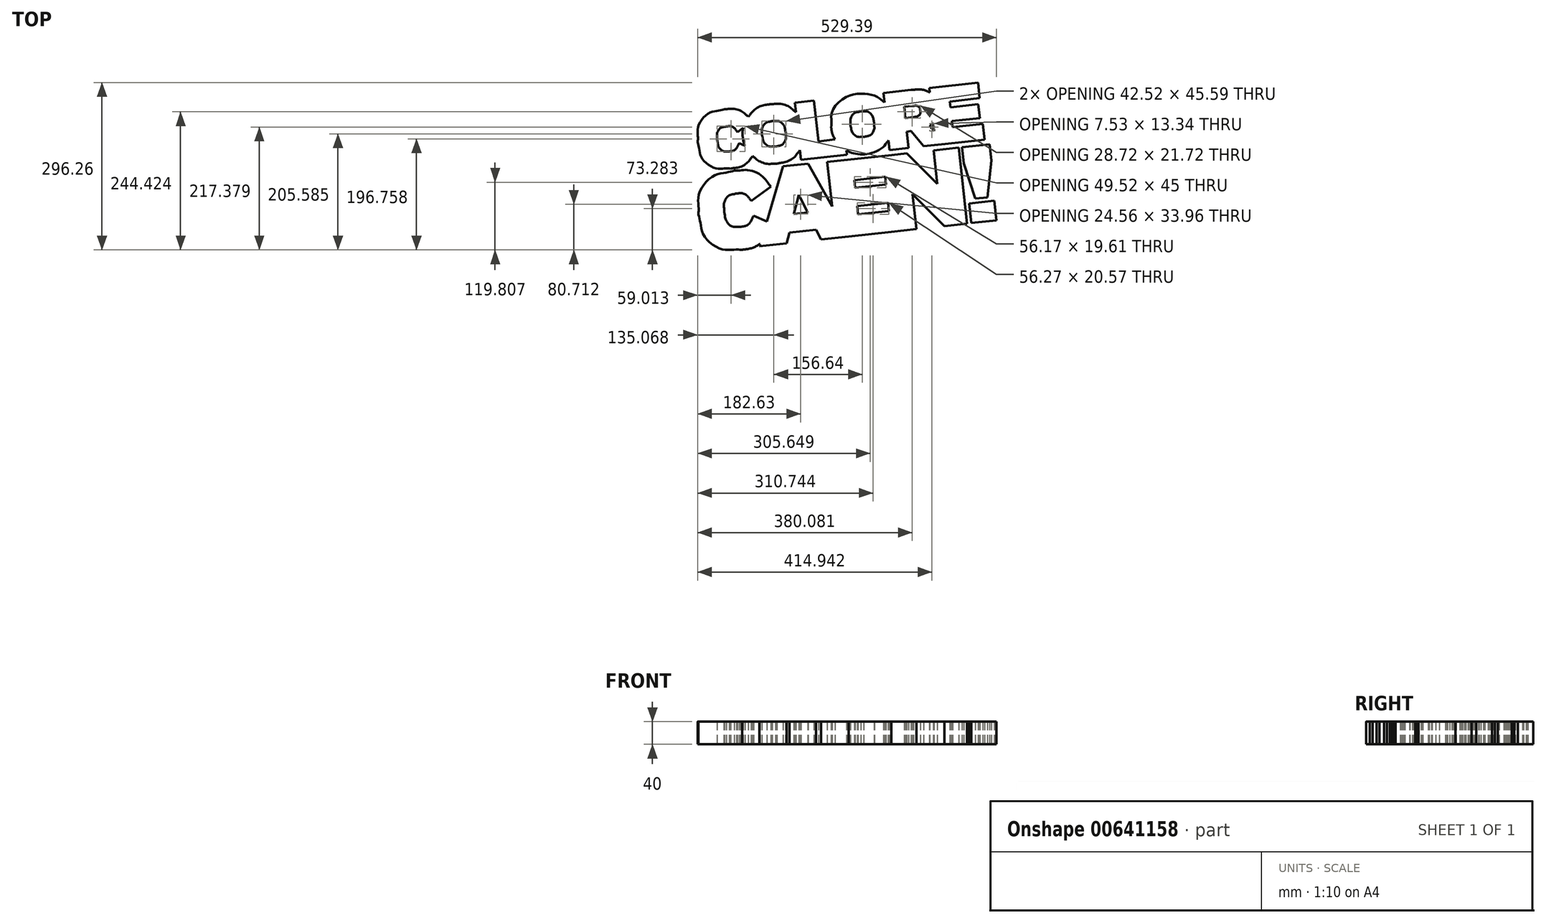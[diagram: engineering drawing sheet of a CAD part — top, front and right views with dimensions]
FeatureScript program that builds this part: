
annotation { "Feature Type Name" : "Feature", "Feature Type Description" : "" }
export const myFeature = defineFeature(function(context is Context, id is Id, definition is map)
    precondition{}
    {
        {
            var Q0;
            Q0=qCreatedBy(makeId("Top.planeOp"),FACE);
            var sketch = newSketch(context, id + "F0", { "sketchPlane" : qUnion([Q0])});
            skLineSegment(sketch, "E0", {"start": v(-194.16, 60.47) * mm, "end": v(-183.95, 68.05) * mm});
            skFitSpline(sketch, "E1", {"points": [v(-213.82, 70.72) * mm, v(-211.03, 70.75) * mm, v(-205.74, 70.82) * mm, v(-198.74, 66.62) * mm, v(-195.71, 62.55) * mm, v(-194.16, 60.47) * mm]});
            skLineSegment(sketch, "E2", {"start": v(-184.83, 51.27) * mm, "end": v(-184.8, 50.98) * mm});
            skFitSpline(sketch, "E3", {"points": [v(-183.95, 68.05) * mm, v(-184.28, 66.24) * mm, v(-184.96, 62.58) * mm, v(-185.27, 56.95) * mm, v(-184.98, 53.18) * mm, v(-184.83, 51.27) * mm]});
            skLineSegment(sketch, "E4", {"start": v(-181.03, 36.4) * mm, "end": v(-191.27, 40.79) * mm});
            skFitSpline(sketch, "E5", {"points": [v(-184.8, 50.98) * mm, v(-184.56, 49.29) * mm, v(-184.1, 45.93) * mm, v(-182.83, 41.04) * mm, v(-181.63, 37.93) * mm, v(-181.03, 36.4) * mm]});
            skFitSpline(sketch, "E6", {"points": [v(-191.27, 40.79) * mm, v(-192.44, 38.32) * mm, v(-194.69, 33.56) * mm, v(-200.78, 27.71) * mm, v(-206.11, 26.6) * mm, v(-208.92, 26) * mm]});
            skLineSegment(sketch, "E7", {"start": v(-230.26, 46.3) * mm, "end": v(-230.3, 46.58) * mm});
            skFitSpline(sketch, "E8", {"points": [v(-208.92, 26) * mm, v(-212.45, 26.2) * mm, v(-219.53, 26.57) * mm, v(-227.86, 35.01) * mm, v(-229.43, 42.36) * mm, v(-230.26, 46.3) * mm]});
            skFitSpline(sketch, "E9", {"points": [v(-230.3, 46.58) * mm, v(-230.3, 50.43) * mm, v(-230.28, 57.75) * mm, v(-224.15, 67.74) * mm, v(-217.27, 69.73) * mm, v(-213.82, 70.72) * mm]});
            skLineSegment(sketch, "E10", {"start": v(-108.67, 59.61) * mm, "end": v(-108.64, 59.32) * mm});
            skFitSpline(sketch, "E11", {"points": [v(-132.37, 80.08) * mm, v(-128.34, 79.88) * mm, v(-120.5, 79.49) * mm, v(-111.39, 70.87) * mm, v(-109.59, 63.41) * mm, v(-108.67, 59.61) * mm]});
            skFitSpline(sketch, "E12", {"points": [v(-108.64, 59.32) * mm, v(-108.7, 55.46) * mm, v(-108.84, 47.9) * mm, v(-115.77, 37.63) * mm, v(-123.25, 35.59) * mm, v(-127.1, 34.53) * mm]});
            skLineSegment(sketch, "E13", {"start": v(-150.8, 55) * mm, "end": v(-150.82, 55.29) * mm});
            skFitSpline(sketch, "E14", {"points": [v(-127.1, 34.53) * mm, v(-131.12, 34.73) * mm, v(-138.96, 35.12) * mm, v(-148.08, 43.74) * mm, v(-149.87, 51.2) * mm, v(-150.8, 55) * mm]});
            skFitSpline(sketch, "E15", {"points": [v(-150.82, 55.29) * mm, v(-150.76, 59.15) * mm, v(-150.62, 66.72) * mm, v(-143.7, 76.98) * mm, v(-136.22, 79.03) * mm, v(-132.37, 80.08) * mm]});
            skLineSegment(sketch, "E16", {"start": v(47.97, 76.77) * mm, "end": v(48, 76.48) * mm});
            skFitSpline(sketch, "E17", {"points": [v(24.27, 97.23) * mm, v(28.3, 97.03) * mm, v(36.14, 96.64) * mm, v(45.25, 88.03) * mm, v(47.05, 80.57) * mm, v(47.97, 76.77) * mm]});
            skFitSpline(sketch, "E18", {"points": [v(48, 76.48) * mm, v(47.93, 72.62) * mm, v(47.8, 65.05) * mm, v(40.87, 54.79) * mm, v(33.4, 52.74) * mm, v(29.55, 51.69) * mm]});
            skLineSegment(sketch, "E19", {"start": v(5.85, 72.15) * mm, "end": v(5.82, 72.44) * mm});
            skFitSpline(sketch, "E20", {"points": [v(29.55, 51.69) * mm, v(25.52, 51.89) * mm, v(17.68, 52.28) * mm, v(8.56, 60.9) * mm, v(6.77, 68.35) * mm, v(5.85, 72.15) * mm]});
            skFitSpline(sketch, "E21", {"points": [v(5.82, 72.44) * mm, v(5.88, 76.3) * mm, v(6.02, 83.87) * mm, v(12.95, 94.13) * mm, v(20.42, 96.18) * mm, v(24.27, 97.23) * mm]});
            skLineSegment(sketch, "E22", {"start": v(129.53, 98.4) * mm, "end": v(129.56, 98.1) * mm});
            skFitSpline(sketch, "E23", {"points": [v(115.64, 106.66) * mm, v(117.94, 106.78) * mm, v(122.1, 107) * mm, v(128.04, 104.07) * mm, v(129.03, 100.3) * mm, v(129.53, 98.4) * mm]});
            skLineSegment(sketch, "E24", {"start": v(117.66, 86.88) * mm, "end": v(103.09, 85.28) * mm});
            skLineSegment(sketch, "E25", {"start": v(103.09, 85.28) * mm, "end": v(100.92, 105.05) * mm});
            skLineSegment(sketch, "E26", {"start": v(100.92, 105.05) * mm, "end": v(115.64, 106.66) * mm});
            skLineSegment(sketch, "E27", {"start": v(152.45, 75.77) * mm, "end": v(153.9, 62.43) * mm});
            skLineSegment(sketch, "E28", {"start": v(153.9, 62.43) * mm, "end": v(146.38, 71.2) * mm});
            skFitSpline(sketch, "E29", {"points": [v(129.56, 98.1) * mm, v(129.48, 96.18) * mm, v(129.3, 92.32) * mm, v(124.19, 88.01) * mm, v(120, 87.29) * mm, v(117.66, 86.88) * mm]});
            skFitSpline(sketch, "E30", {"points": [v(146.38, 71.2) * mm, v(147.1, 71.66) * mm, v(148.53, 72.6) * mm, v(150.56, 74.12) * mm, v(151.82, 75.22) * mm, v(152.45, 75.77) * mm]});
            skFitSpline(sketch, "E31", {"points": [v(-206.47, -4.38) * mm, v(-200.69, -3.35) * mm, v(-190, -1.46) * mm, v(-176.33, 6.53) * mm, v(-170.32, 14.02) * mm, v(-167.44, 17.61) * mm]});
            skFitSpline(sketch, "E32", {"points": [v(-167.44, 17.61) * mm, v(-163.43, 14.68) * mm, v(-155.28, 8.71) * mm, v(-140.1, 4.13) * mm, v(-129.54, 4.47) * mm, v(-124.1, 4.64) * mm]});
            skLineSegment(sketch, "E33", {"start": v(-83.36, 28.4) * mm, "end": v(-81.5, 11.5) * mm});
            skLineSegment(sketch, "E34", {"start": v(-81.5, 11.5) * mm, "end": v(-0.3, 20.4) * mm});
            skLineSegment(sketch, "E35", {"start": v(-0.3, 20.4) * mm, "end": v(-1.14, 28.1) * mm});
            skFitSpline(sketch, "E36", {"points": [v(-124.1, 4.64) * mm, v(-118.54, 5.71) * mm, v(-107.7, 7.8) * mm, v(-93.39, 16.22) * mm, v(-86.67, 24.39) * mm, v(-83.36, 28.4) * mm]});
            skLineSegment(sketch, "E37", {"start": v(73.28, 45.56) * mm, "end": v(75.13, 28.65) * mm});
            skLineSegment(sketch, "E38", {"start": v(75.13, 28.65) * mm, "end": v(108.88, 32.35) * mm});
            skLineSegment(sketch, "E39", {"start": v(108.88, 32.35) * mm, "end": v(105.73, 61.2) * mm});
            skLineSegment(sketch, "E40", {"start": v(105.73, 61.2) * mm, "end": v(112.65, 61.95) * mm});
            skLineSegment(sketch, "E41", {"start": v(112.65, 61.95) * mm, "end": v(112.94, 61.99) * mm});
            skLineSegment(sketch, "E42", {"start": v(112.94, 61.99) * mm, "end": v(135.14, 35.22) * mm});
            skLineSegment(sketch, "E43", {"start": v(135.14, 35.22) * mm, "end": v(173.65, 39.44) * mm});
            skLineSegment(sketch, "E44", {"start": v(173.65, 39.44) * mm, "end": v(243.46, 47.09) * mm});
            skLineSegment(sketch, "E45", {"start": v(243.46, 47.09) * mm, "end": v(240.43, 74.78) * mm});
            skLineSegment(sketch, "E46", {"start": v(240.43, 74.78) * mm, "end": v(186.77, 68.9) * mm});
            skLineSegment(sketch, "E47", {"start": v(186.77, 68.9) * mm, "end": v(185.57, 79.87) * mm});
            skLineSegment(sketch, "E48", {"start": v(185.57, 79.87) * mm, "end": v(234.9, 85.27) * mm});
            skLineSegment(sketch, "E49", {"start": v(234.9, 85.27) * mm, "end": v(232.23, 109.65) * mm});
            skLineSegment(sketch, "E50", {"start": v(232.23, 109.65) * mm, "end": v(182.9, 104.24) * mm});
            skLineSegment(sketch, "E51", {"start": v(182.9, 104.24) * mm, "end": v(181.78, 114.48) * mm});
            skLineSegment(sketch, "E52", {"start": v(181.78, 114.48) * mm, "end": v(234.72, 120.28) * mm});
            skLineSegment(sketch, "E53", {"start": v(234.72, 120.28) * mm, "end": v(231.68, 147.98) * mm});
            skLineSegment(sketch, "E54", {"start": v(231.68, 147.98) * mm, "end": v(145.57, 138.55) * mm});
            skLineSegment(sketch, "E55", {"start": v(145.57, 138.55) * mm, "end": v(146.45, 130.5) * mm});
            skFitSpline(sketch, "E56", {"points": [v(-1.14, 28.1) * mm, v(2.24, 26.53) * mm, v(9.1, 23.33) * mm, v(20.62, 21.28) * mm, v(34.2, 21.4) * mm, v(48.91, 25.15) * mm, v(63.26, 33.33) * mm, v(69.97, 41.53) * mm, v(73.28, 45.56) * mm]});
            skLineSegment(sketch, "E57", {"start": v(113.4, 135.02) * mm, "end": v(64.07, 129.62) * mm});
            skLineSegment(sketch, "E58", {"start": v(64.07, 129.62) * mm, "end": v(65.9, 113) * mm});
            skFitSpline(sketch, "E59", {"points": [v(146.45, 130.5) * mm, v(143.59, 131.78) * mm, v(137.35, 134.55) * mm, v(126, 135.92) * mm, v(117.86, 135.34) * mm, v(113.4, 135.02) * mm]});
            skLineSegment(sketch, "E60", {"start": v(-28.2, 68.43) * mm, "end": v(-28.16, 68.14) * mm});
            skFitSpline(sketch, "E61", {"points": [v(65.9, 113) * mm, v(61.83, 116.19) * mm, v(53.56, 122.65) * mm, v(37.89, 127.41) * mm, v(17.05, 128.04) * mm, v(-6.85, 119.36) * mm, v(-26.8, 96.8) * mm, v(-27.72, 77.93) * mm, v(-28.2, 68.43) * mm]});
            skLineSegment(sketch, "E62", {"start": v(-21.24, 47.3) * mm, "end": v(-50.91, 44.04) * mm});
            skLineSegment(sketch, "E63", {"start": v(-50.91, 44.04) * mm, "end": v(-58.81, 116.16) * mm});
            skLineSegment(sketch, "E64", {"start": v(-58.81, 116.16) * mm, "end": v(-92.57, 112.47) * mm});
            skLineSegment(sketch, "E65", {"start": v(-92.57, 112.47) * mm, "end": v(-90.75, 95.85) * mm});
            skFitSpline(sketch, "E66", {"points": [v(-28.16, 68.14) * mm, v(-27.78, 65.65) * mm, v(-27.03, 60.73) * mm, v(-24.68, 53.7) * mm, v(-22.38, 49.41) * mm, v(-21.24, 47.3) * mm]});
            skFitSpline(sketch, "E67", {"points": [v(-90.75, 95.85) * mm, v(-94.81, 99.02) * mm, v(-103.08, 105.45) * mm, v(-118.77, 110.46) * mm, v(-129.72, 110.13) * mm, v(-135.35, 109.97) * mm]});
            skFitSpline(sketch, "E68", {"points": [v(-135.35, 109.97) * mm, v(-140.7, 108.96) * mm, v(-151.09, 107) * mm, v(-164.93, 99.18) * mm, v(-171.64, 91.57) * mm, v(-174.94, 87.82) * mm]});
            skFitSpline(sketch, "E69", {"points": [v(-174.94, 87.82) * mm, v(-178.57, 90.78) * mm, v(-186.02, 96.86) * mm, v(-200.75, 101.66) * mm, v(-211.18, 101.27) * mm, v(-216.7, 101.06) * mm]});
            skLineSegment(sketch, "E70", {"start": v(-264.6, 42.54) * mm, "end": v(-264.56, 42.25) * mm});
            skFitSpline(sketch, "E71", {"points": [v(-216.7, 101.06) * mm, v(-226.02, 98.7) * mm, v(-244.18, 94.09) * mm, v(-263.51, 70.81) * mm, v(-264.23, 52.1) * mm, v(-264.6, 42.54) * mm]});
            skLineSegment(sketch, "E72", {"start": v(206.42, 4.7) * mm, "end": v(226.82, -57.52) * mm});
            skLineSegment(sketch, "E73", {"start": v(226.82, -57.52) * mm, "end": v(248.7, -55.12) * mm});
            skLineSegment(sketch, "E74", {"start": v(248.7, -55.12) * mm, "end": v(255.15, 10.04) * mm});
            skLineSegment(sketch, "E75", {"start": v(255.15, 10.04) * mm, "end": v(252, 38.82) * mm});
            skLineSegment(sketch, "E76", {"start": v(252, 38.82) * mm, "end": v(203.27, 33.48) * mm});
            skLineSegment(sketch, "E77", {"start": v(203.27, 33.48) * mm, "end": v(206.42, 4.7) * mm});
            skLineSegment(sketch, "E78", {"start": v(19.4, -85.28) * mm, "end": v(17.8, -70.7) * mm});
            skLineSegment(sketch, "E79", {"start": v(17.8, -70.7) * mm, "end": v(72.48, -64.71) * mm});
            skLineSegment(sketch, "E80", {"start": v(72.48, -64.71) * mm, "end": v(74.08, -79.3) * mm});
            skLineSegment(sketch, "E81", {"start": v(74.08, -79.3) * mm, "end": v(19.4, -85.28) * mm});
            skLineSegment(sketch, "E82", {"start": v(12.76, -24.66) * mm, "end": v(67.44, -18.67) * mm});
            skLineSegment(sketch, "E83", {"start": v(67.44, -18.67) * mm, "end": v(68.93, -32.29) * mm});
            skLineSegment(sketch, "E84", {"start": v(68.93, -32.29) * mm, "end": v(14.26, -38.28) * mm});
            skLineSegment(sketch, "E85", {"start": v(14.26, -38.28) * mm, "end": v(12.76, -24.66) * mm});
            skLineSegment(sketch, "E86", {"start": v(-94.45, -84.55) * mm, "end": v(-85.74, -50.59) * mm});
            skLineSegment(sketch, "E87", {"start": v(-85.74, -50.59) * mm, "end": v(-69.9, -81.86) * mm});
            skLineSegment(sketch, "E88", {"start": v(-69.9, -81.86) * mm, "end": v(-94.45, -84.55) * mm});
            skLineSegment(sketch, "E89", {"start": v(153.2, 28) * mm, "end": v(159.69, -31.28) * mm});
            skLineSegment(sketch, "E90", {"start": v(159.69, -31.28) * mm, "end": v(105.42, 22.77) * mm});
            skLineSegment(sketch, "E91", {"start": v(105.42, 22.77) * mm, "end": v(79.14, 19.9) * mm});
            skLineSegment(sketch, "E92", {"start": v(79.14, 19.9) * mm, "end": v(79.14, 19.9) * mm});
            skLineSegment(sketch, "E93", {"start": v(79.14, 19.9) * mm, "end": v(-35.4, 7.35) * mm});
            skLineSegment(sketch, "E94", {"start": v(-35.4, 7.35) * mm, "end": v(-26.76, -71.47) * mm});
            skLineSegment(sketch, "E95", {"start": v(-26.76, -71.47) * mm, "end": v(-68.88, 4.65) * mm});
            skLineSegment(sketch, "E96", {"start": v(-68.88, 4.65) * mm, "end": v(-113.4, -0.22) * mm});
            skLineSegment(sketch, "E97", {"start": v(-113.4, -0.22) * mm, "end": v(-142.28, -98.02) * mm});
            skLineSegment(sketch, "E98", {"start": v(-142.28, -98.02) * mm, "end": v(-165.88, -87.9) * mm});
            skFitSpline(sketch, "E99", {"points": [v(-264.56, 42.25) * mm, v(-262.1, 32.81) * mm, v(-257.39, 14.65) * mm, v(-233.72, -3.46) * mm, v(-215.6, -4.07) * mm, v(-206.47, -4.38) * mm]});
            skFitSpline(sketch, "E100", {"points": [v(-165.88, -87.9) * mm, v(-167.43, -91.18) * mm, v(-170.42, -97.52) * mm, v(-178.52, -105.3) * mm, v(-185.62, -106.78) * mm, v(-189.35, -107.56) * mm]});
            skLineSegment(sketch, "E101", {"start": v(-217.74, -80.58) * mm, "end": v(-217.78, -80.2) * mm});
            skFitSpline(sketch, "E102", {"points": [v(-189.35, -107.56) * mm, v(-194.05, -107.31) * mm, v(-203.46, -106.81) * mm, v(-214.55, -95.58) * mm, v(-216.63, -85.82) * mm, v(-217.74, -80.58) * mm]});
            skFitSpline(sketch, "E103", {"points": [v(-217.78, -80.2) * mm, v(-217.78, -75.08) * mm, v(-217.77, -65.34) * mm, v(-209.6, -52.05) * mm, v(-200.46, -49.41) * mm, v(-195.87, -48.09) * mm]});
            skLineSegment(sketch, "E104", {"start": v(-169.71, -61.73) * mm, "end": v(-135.06, -36) * mm});
            skFitSpline(sketch, "E105", {"points": [v(-195.87, -48.09) * mm, v(-192.16, -48.04) * mm, v(-185.12, -47.96) * mm, v(-175.81, -53.54) * mm, v(-171.78, -58.95) * mm, v(-169.71, -61.73) * mm]});
            skFitSpline(sketch, "E106", {"points": [v(-135.06, -36) * mm, v(-140.09, -30.03) * mm, v(-150.26, -17.97) * mm, v(-173.6, -7.17) * mm, v(-190.64, -7.54) * mm, v(-199.7, -7.73) * mm]});
            skLineSegment(sketch, "E107", {"start": v(-263.4, -85.58) * mm, "end": v(-263.36, -85.96) * mm});
            skFitSpline(sketch, "E108", {"points": [v(-199.7, -7.73) * mm, v(-212.1, -10.88) * mm, v(-236.25, -17) * mm, v(-261.97, -47.97) * mm, v(-262.92, -72.85) * mm, v(-263.4, -85.58) * mm]});
            skFitSpline(sketch, "E109", {"points": [v(-263.36, -85.96) * mm, v(-260.1, -98.5) * mm, v(-253.82, -122.67) * mm, v(-222.34, -146.76) * mm, v(-198.25, -147.57) * mm, v(-186.1, -147.98) * mm]});
            skLineSegment(sketch, "E110", {"start": v(-154, -137.67) * mm, "end": v(-155.17, -141.68) * mm});
            skLineSegment(sketch, "E111", {"start": v(-155.17, -141.68) * mm, "end": v(-107.21, -136.43) * mm});
            skLineSegment(sketch, "E112", {"start": v(-107.21, -136.43) * mm, "end": v(-102.28, -117.63) * mm});
            skLineSegment(sketch, "E113", {"start": v(-102.28, -117.63) * mm, "end": v(-55.28, -112.49) * mm});
            skLineSegment(sketch, "E114", {"start": v(-55.28, -112.49) * mm, "end": v(-46.2, -129.74) * mm});
            skLineSegment(sketch, "E115", {"start": v(-46.2, -129.74) * mm, "end": v(2.53, -124.4) * mm});
            skLineSegment(sketch, "E116", {"start": v(2.53, -124.4) * mm, "end": v(2.53, -124.4) * mm});
            skLineSegment(sketch, "E117", {"start": v(2.53, -124.4) * mm, "end": v(78.11, -116.13) * mm});
            skLineSegment(sketch, "E118", {"start": v(78.11, -116.13) * mm, "end": v(78.11, -116.13) * mm});
            skLineSegment(sketch, "E119", {"start": v(78.11, -116.13) * mm, "end": v(122.62, -111.25) * mm});
            skLineSegment(sketch, "E120", {"start": v(122.62, -111.25) * mm, "end": v(115.84, -49.29) * mm});
            skLineSegment(sketch, "E121", {"start": v(115.84, -49.29) * mm, "end": v(172.5, -105.8) * mm});
            skLineSegment(sketch, "E122", {"start": v(172.5, -105.8) * mm, "end": v(212.41, -101.42) * mm});
            skLineSegment(sketch, "E123", {"start": v(212.41, -101.42) * mm, "end": v(197.7, 32.88) * mm});
            skLineSegment(sketch, "E124", {"start": v(197.7, 32.88) * mm, "end": v(153.2, 28) * mm});
            skLineSegment(sketch, "E125", {"start": v(260.81, -61.17) * mm, "end": v(216.3, -66.05) * mm});
            skLineSegment(sketch, "E126", {"start": v(216.3, -66.05) * mm, "end": v(220.08, -100.58) * mm});
            skLineSegment(sketch, "E127", {"start": v(220.08, -100.58) * mm, "end": v(264.6, -95.7) * mm});
            skLineSegment(sketch, "E128", {"start": v(264.6, -95.7) * mm, "end": v(260.81, -61.17) * mm});
            skFitSpline(sketch, "E129", {"points": [v(-186.1, -147.98) * mm, v(-182, -147.38) * mm, v(-174.2, -146.24) * mm, v(-163.34, -142.77) * mm, v(-157.02, -139.32) * mm, v(-154, -137.67) * mm]});
            skSolve(sketch);
        }
        {
            var Q0;
            Q0=makeQuery(id+"F0.imprint","IMPRINT",FACE,{"disambiguationData":[TD([[makeQuery(id+"F0.imprint","IMPRINT",EDGE,{"derivedFrom":sQuery(id+"F0.wireOp",EDGE,"E78")}),1.0]])]});
            var Q1;
            Q1=makeQuery(id+"F0.imprint","IMPRINT",FACE,{"disambiguationData":[TD([[makeQuery(id+"F0.imprint","IMPRINT",EDGE,{"derivedFrom":sQuery(id+"F0.wireOp",EDGE,"E0")}),1.0]])]});
            var Q2;
            Q2=makeQuery(id+"F0.imprint","IMPRINT",FACE,{"disambiguationData":[TD([[makeQuery(id+"F0.imprint","IMPRINT",EDGE,{"derivedFrom":sQuery(id+"F0.wireOp",EDGE,"E72")}),1.0]])]});
            var Q3;
            Q3=makeQuery(id+"F0.imprint","IMPRINT",FACE,{"disambiguationData":[TD([[makeQuery(id+"F0.imprint","IMPRINT",EDGE,{"derivedFrom":sQuery(id+"F0.wireOp",EDGE,"E125")}),1.0]])]});
            extrude(context, id + "F1", {"entities" : qUnion([Q0, Q1, Q2, Q3]), "depth" : 40 * mm, "offsetDistance" : 25 * mm});
        }
        {
            var Q0;
            Q0=makeQuery(id+"F1.opExtrude","SWEPT_BODY",BODY,{"disambiguationData":[OSD([sQuery(id+"F0.wireOp",EDGE,"E72"),sQuery(id+"F0.wireOp",EDGE,"E73"),sQuery(id+"F0.wireOp",EDGE,"E74"),sQuery(id+"F0.wireOp",EDGE,"E75"),sQuery(id+"F0.wireOp",EDGE,"E76"),sQuery(id+"F0.wireOp",EDGE,"E77")])]});
            deleteBodies(context, id + "F2", {"entities" : qUnion([Q0])});
        }
        {
            var Q0;
            Q0=makeQuery(id+"F0.imprint","IMPRINT",FACE,{"disambiguationData":[TD([[makeQuery(id+"F0.imprint","IMPRINT",EDGE,{"derivedFrom":sQuery(id+"F0.wireOp",EDGE,"E72")}),1.0]])]});
            extrude(context, id + "F3", {"entities" : qUnion([Q0]), "depth" : 40 * mm, "offsetDistance" : 25 * mm});
        }
    });
